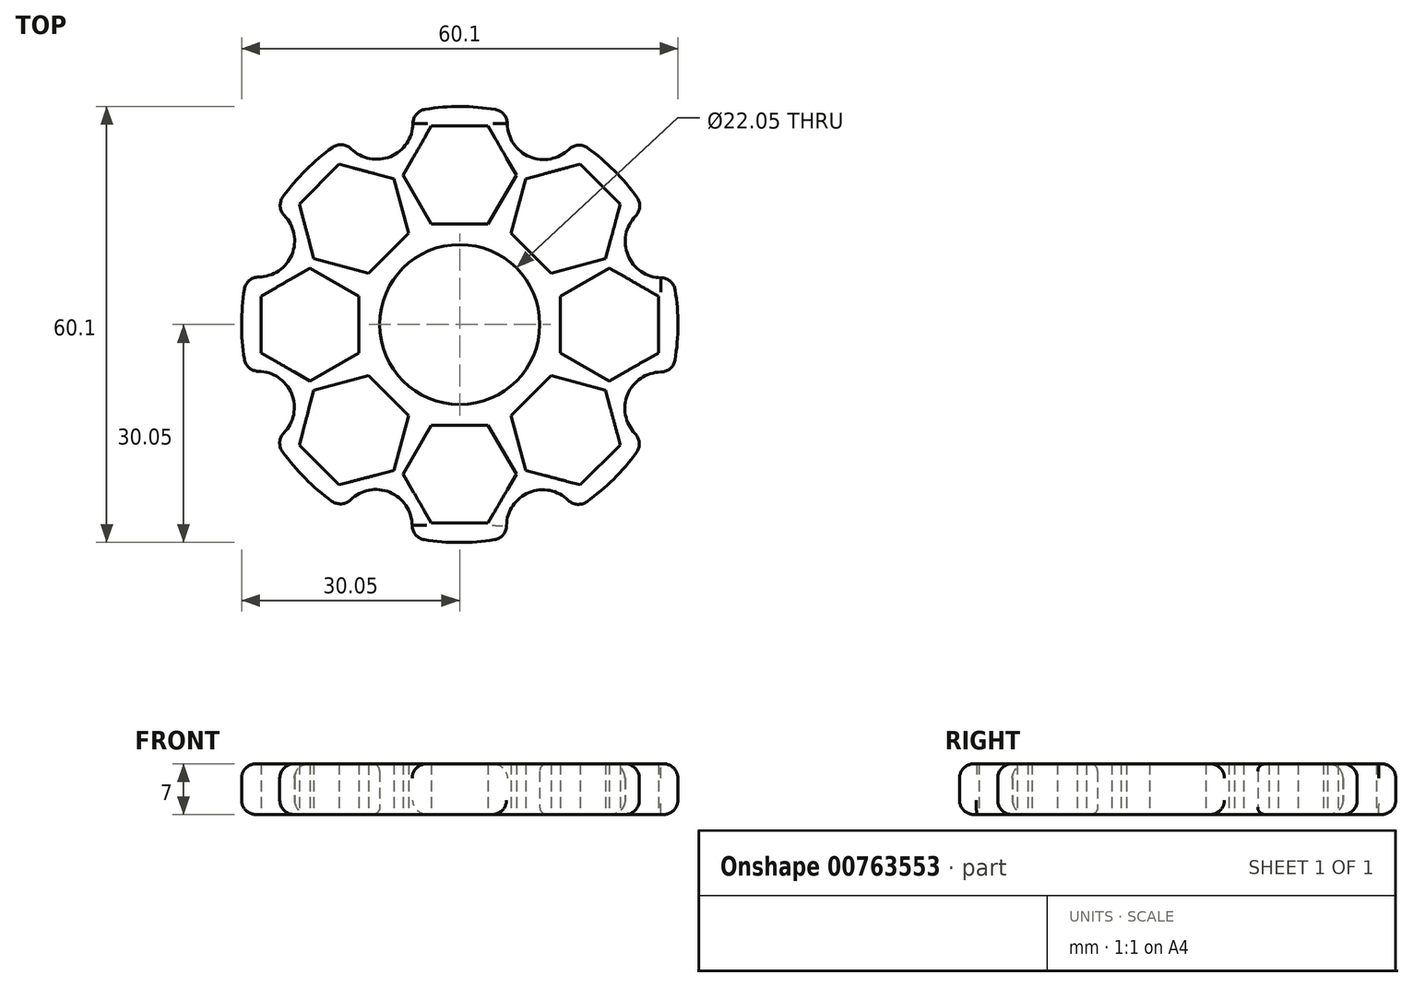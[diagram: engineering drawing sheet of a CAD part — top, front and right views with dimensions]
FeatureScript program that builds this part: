
annotation { "Feature Type Name" : "Feature", "Feature Type Description" : "" }
export const myFeature = defineFeature(function(context is Context, id is Id, definition is map)
    precondition{}
    {
        {
            var Q0;
            Q0=qCreatedBy(makeId("Top.planeOp"),FACE);
            var sketch = newSketch(context, id + "F0", { "sketchPlane" : qUnion([Q0])});
            skCircle(sketch, "E0", {"center": v(0, 0) * mm, "radius": 11.03 * mm});
            skCircle(sketch, "E1", {"center": v(0, 0) * mm, "radius": 13.53 * mm});
            skCircle(sketch, "E2", {"center": v(0, 0) * mm, "radius": 30.05 * mm});
            skLineSegment(sketch, "E3.0", {"start": v(3.9, 13.87) * mm, "end": v(-3.9, 13.87) * mm});
            skLineSegment(sketch, "E3.1", {"start": v(-3.9, 13.87) * mm, "end": v(-7.8, 20.62) * mm});
            skLineSegment(sketch, "E3.2", {"start": v(-7.8, 20.62) * mm, "end": v(-3.9, 27.37) * mm});
            skLineSegment(sketch, "E3.3", {"start": v(-3.9, 27.37) * mm, "end": v(3.9, 27.37) * mm});
            skLineSegment(sketch, "E3.4", {"start": v(3.9, 27.37) * mm, "end": v(7.8, 20.62) * mm});
            skLineSegment(sketch, "E3.5", {"start": v(7.8, 20.62) * mm, "end": v(3.9, 13.87) * mm});
            skPoint(sketch, "E3.0.midPoint", {"position": v(0, 13.87) * mm});
            skLineSegment(sketch, "E4.1.0", {"start": v(-9.07, 20.09) * mm, "end": v(-7.05, 12.56) * mm});
            skLineSegment(sketch, "E4.1.1", {"start": v(-20.09, 9.07) * mm, "end": v(-22.1, 16.6) * mm});
            skLineSegment(sketch, "E4.1.2", {"start": v(-12.56, 7.05) * mm, "end": v(-20.09, 9.07) * mm});
            skLineSegment(sketch, "E4.1.3", {"start": v(-7.05, 12.56) * mm, "end": v(-12.56, 7.05) * mm});
            skLineSegment(sketch, "E4.1.4", {"start": v(-22.1, 16.6) * mm, "end": v(-16.6, 22.1) * mm});
            skLineSegment(sketch, "E4.1.5", {"start": v(-16.6, 22.1) * mm, "end": v(-9.07, 20.09) * mm});
            skPoint(sketch, "E4.1.6", {"position": v(-9.8, 9.8) * mm});
            skLineSegment(sketch, "E4.2.0", {"start": v(-20.62, 7.8) * mm, "end": v(-13.87, 3.9) * mm});
            skLineSegment(sketch, "E4.2.1", {"start": v(-20.62, -7.8) * mm, "end": v(-27.37, -3.9) * mm});
            skLineSegment(sketch, "E4.2.2", {"start": v(-13.87, -3.9) * mm, "end": v(-20.62, -7.8) * mm});
            skLineSegment(sketch, "E4.2.3", {"start": v(-13.87, 3.9) * mm, "end": v(-13.87, -3.9) * mm});
            skLineSegment(sketch, "E4.2.4", {"start": v(-27.37, -3.9) * mm, "end": v(-27.37, 3.9) * mm});
            skLineSegment(sketch, "E4.2.5", {"start": v(-27.37, 3.9) * mm, "end": v(-20.62, 7.8) * mm});
            skPoint(sketch, "E4.2.6", {"position": v(-13.87, 0) * mm});
            skLineSegment(sketch, "E4.3.0", {"start": v(-20.09, -9.07) * mm, "end": v(-12.56, -7.05) * mm});
            skLineSegment(sketch, "E4.3.1", {"start": v(-9.07, -20.09) * mm, "end": v(-16.6, -22.1) * mm});
            skLineSegment(sketch, "E4.3.2", {"start": v(-7.05, -12.56) * mm, "end": v(-9.07, -20.09) * mm});
            skLineSegment(sketch, "E4.3.3", {"start": v(-12.56, -7.05) * mm, "end": v(-7.05, -12.56) * mm});
            skLineSegment(sketch, "E4.3.4", {"start": v(-16.6, -22.1) * mm, "end": v(-22.1, -16.6) * mm});
            skLineSegment(sketch, "E4.3.5", {"start": v(-22.1, -16.6) * mm, "end": v(-20.09, -9.07) * mm});
            skPoint(sketch, "E4.3.6", {"position": v(-9.8, -9.8) * mm});
            skLineSegment(sketch, "E4.4.0", {"start": v(-7.8, -20.62) * mm, "end": v(-3.9, -13.87) * mm});
            skLineSegment(sketch, "E4.4.1", {"start": v(7.8, -20.62) * mm, "end": v(3.9, -27.37) * mm});
            skLineSegment(sketch, "E4.4.2", {"start": v(3.9, -13.87) * mm, "end": v(7.8, -20.62) * mm});
            skLineSegment(sketch, "E4.4.3", {"start": v(-3.9, -13.87) * mm, "end": v(3.9, -13.87) * mm});
            skLineSegment(sketch, "E4.4.4", {"start": v(3.9, -27.37) * mm, "end": v(-3.9, -27.37) * mm});
            skLineSegment(sketch, "E4.4.5", {"start": v(-3.9, -27.37) * mm, "end": v(-7.8, -20.62) * mm});
            skPoint(sketch, "E4.4.6", {"position": v(0, -13.87) * mm});
            skLineSegment(sketch, "E4.5.0", {"start": v(9.07, -20.09) * mm, "end": v(7.05, -12.56) * mm});
            skLineSegment(sketch, "E4.5.1", {"start": v(20.09, -9.07) * mm, "end": v(22.1, -16.6) * mm});
            skLineSegment(sketch, "E4.5.2", {"start": v(12.56, -7.05) * mm, "end": v(20.09, -9.07) * mm});
            skLineSegment(sketch, "E4.5.3", {"start": v(7.05, -12.56) * mm, "end": v(12.56, -7.05) * mm});
            skLineSegment(sketch, "E4.5.4", {"start": v(22.1, -16.6) * mm, "end": v(16.6, -22.1) * mm});
            skLineSegment(sketch, "E4.5.5", {"start": v(16.6, -22.1) * mm, "end": v(9.07, -20.09) * mm});
            skPoint(sketch, "E4.5.6", {"position": v(9.8, -9.8) * mm});
            skLineSegment(sketch, "E4.6.0", {"start": v(20.62, -7.8) * mm, "end": v(13.87, -3.9) * mm});
            skLineSegment(sketch, "E4.6.1", {"start": v(20.62, 7.8) * mm, "end": v(27.37, 3.9) * mm});
            skLineSegment(sketch, "E4.6.2", {"start": v(13.87, 3.9) * mm, "end": v(20.62, 7.8) * mm});
            skLineSegment(sketch, "E4.6.3", {"start": v(13.87, -3.9) * mm, "end": v(13.87, 3.9) * mm});
            skLineSegment(sketch, "E4.6.4", {"start": v(27.37, 3.9) * mm, "end": v(27.37, -3.9) * mm});
            skLineSegment(sketch, "E4.6.5", {"start": v(27.37, -3.9) * mm, "end": v(20.62, -7.8) * mm});
            skPoint(sketch, "E4.6.6", {"position": v(13.87, 0) * mm});
            skLineSegment(sketch, "E4.7.0", {"start": v(20.09, 9.07) * mm, "end": v(12.56, 7.05) * mm});
            skLineSegment(sketch, "E4.7.1", {"start": v(9.07, 20.09) * mm, "end": v(16.6, 22.1) * mm});
            skLineSegment(sketch, "E4.7.2", {"start": v(7.05, 12.56) * mm, "end": v(9.07, 20.09) * mm});
            skLineSegment(sketch, "E4.7.3", {"start": v(12.56, 7.05) * mm, "end": v(7.05, 12.56) * mm});
            skLineSegment(sketch, "E4.7.4", {"start": v(16.6, 22.1) * mm, "end": v(22.1, 16.6) * mm});
            skLineSegment(sketch, "E4.7.5", {"start": v(22.1, 16.6) * mm, "end": v(20.09, 9.07) * mm});
            skPoint(sketch, "E4.7.6", {"position": v(9.8, 9.8) * mm});
            skPoint(sketch, "E5.centerSnap0", {"position": v(-11.44, 27.63) * mm});
            skCircle(sketch, "E6", {"center": v(-11.44, 27.78) * mm, "radius": 5 * mm});
            skCircle(sketch, "E7.1.0", {"center": v(-27.74, 11.55) * mm, "radius": 5 * mm});
            skCircle(sketch, "E7.2.0", {"center": v(-27.78, -11.44) * mm, "radius": 5 * mm});
            skCircle(sketch, "E7.3.0", {"center": v(-11.55, -27.74) * mm, "radius": 5 * mm});
            skCircle(sketch, "E7.4.0", {"center": v(11.44, -27.78) * mm, "radius": 5 * mm});
            skCircle(sketch, "E7.5.0", {"center": v(27.74, -11.55) * mm, "radius": 5 * mm});
            skCircle(sketch, "E7.6.0", {"center": v(27.78, 11.44) * mm, "radius": 5 * mm});
            skCircle(sketch, "E7.7.0", {"center": v(11.55, 27.74) * mm, "radius": 5 * mm});
            skSolve(sketch);
        }
        {
            var Q0;
            Q0=makeQuery(id+"F0.imprint","IMPRINT",FACE,{"disambiguationData":[TD([[makeQuery(id+"F0.imprint","IMPRINT",EDGE,{"derivedFrom":sQuery(id+"F0.wireOp",EDGE,"E1")}),-1.0]])]});
            var Q1;
            Q1=makeQuery(id+"F0.imprint","IMPRINT",FACE,{"disambiguationData":[TD([[makeQuery(id+"F0.imprint","IMPRINT",EDGE,{"derivedFrom":sQuery(id+"F0.wireOp",EDGE,"E0")}),-1.0]])]});
            extrude(context, id + "F1", {"entities" : qUnion([Q0, Q1]), "depth" : 7 * mm, "offsetDistance" : 25 * mm});
        }
        {
            var Q0;
            {var subQ0=sQuery(id+"F0.wireOp",EDGE,"E2");Q0=makeQuery(id+"F1.opExtrude","CAP_EDGE",EDGE,{"disambiguationData":[OSD([subQ0]),TDD([makeQuery(id+"F0.imprint","IMPRINT",EDGE,{"disambiguationData":[TD([[makeQuery(id+"F0.imprint","INTERSECT",VERTEX,{"disambiguationData":[OD(1.0)],"derivedFrom":[subQ0,sQuery(id+"F0.wireOp",EDGE,"E7.3.0")]}),-1.0]])],"derivedFrom":subQ0})])],"isStart":true});}
            var Q1;
            Q1=makeQuery(id+"F1.opExtrude","CAP_EDGE",EDGE,{"disambiguationData":[OSD([sQuery(id+"F0.wireOp",EDGE,"E7.3.0")])],"isStart":true});
            var Q2;
            Q2=makeQuery(id+"F1.opExtrude","CAP_EDGE",EDGE,{"disambiguationData":[OSD([sQuery(id+"F0.wireOp",EDGE,"E7.2.0")])],"isStart":true});
            var Q3;
            {var subQ0=sQuery(id+"F0.wireOp",EDGE,"E2");Q3=makeQuery(id+"F1.opExtrude","CAP_EDGE",EDGE,{"disambiguationData":[OSD([subQ0]),TDD([makeQuery(id+"F0.imprint","IMPRINT",EDGE,{"disambiguationData":[TD([[makeQuery(id+"F0.imprint","INTERSECT",VERTEX,{"disambiguationData":[OD(1.0)],"derivedFrom":[subQ0,sQuery(id+"F0.wireOp",EDGE,"E7.1.0")]}),-1.0]])],"derivedFrom":subQ0})])],"isStart":true});}
            var Q4;
            {var subQ0=sQuery(id+"F0.wireOp",EDGE,"E7.1.0");var subQ1=sQuery(id+"F0.wireOp",EDGE,"E2");Q4=makeQuery(id+"F1.opExtrude","SWEPT_EDGE",EDGE,{"disambiguationData":[OSD([subQ1,subQ0]),TDD([makeQuery(id+"F0.imprint","INTERSECT",VERTEX,{"disambiguationData":[OD(0.0)],"derivedFrom":[subQ1,subQ0]})])]});}
            var Q5;
            {var subQ0=sQuery(id+"F0.wireOp",EDGE,"E7.1.0");var subQ1=sQuery(id+"F0.wireOp",EDGE,"E2");Q5=makeQuery(id+"F1.opExtrude","SWEPT_EDGE",EDGE,{"disambiguationData":[OSD([subQ1,subQ0]),TDD([makeQuery(id+"F0.imprint","INTERSECT",VERTEX,{"disambiguationData":[OD(1.0)],"derivedFrom":[subQ1,subQ0]})])]});}
            var Q6;
            {var subQ0=sQuery(id+"F0.wireOp",EDGE,"E2");Q6=makeQuery(id+"F1.opExtrude","CAP_EDGE",EDGE,{"disambiguationData":[OSD([subQ0]),TDD([makeQuery(id+"F0.imprint","IMPRINT",EDGE,{"disambiguationData":[TD([[makeQuery(id+"F0.imprint","INTERSECT",VERTEX,{"disambiguationData":[OD(1.0)],"derivedFrom":[subQ0,sQuery(id+"F0.wireOp",EDGE,"E7.2.0")]}),-1.0]])],"derivedFrom":subQ0})])],"isStart":true});}
            var Q7;
            Q7=makeQuery(id+"F1.opExtrude","CAP_EDGE",EDGE,{"disambiguationData":[OSD([sQuery(id+"F0.wireOp",EDGE,"E7.1.0")])],"isStart":true});
            var Q8;
            {var subQ0=sQuery(id+"F0.wireOp",EDGE,"E2");Q8=makeQuery(id+"F1.opExtrude","CAP_EDGE",EDGE,{"disambiguationData":[OSD([subQ0]),TDD([makeQuery(id+"F0.imprint","IMPRINT",EDGE,{"disambiguationData":[TD([[makeQuery(id+"F0.imprint","INTERSECT",VERTEX,{"disambiguationData":[OD(1.0)],"derivedFrom":[subQ0,sQuery(id+"F0.wireOp",EDGE,"E6")]}),-1.0]])],"derivedFrom":subQ0})])],"isStart":true});}
            var Q9;
            Q9=makeQuery(id+"F1.opExtrude","CAP_EDGE",EDGE,{"disambiguationData":[OSD([sQuery(id+"F0.wireOp",EDGE,"E6")])],"isStart":true});
            var Q10;
            {var subQ0=sQuery(id+"F0.wireOp",EDGE,"E2");Q10=makeQuery(id+"F1.opExtrude","CAP_EDGE",EDGE,{"disambiguationData":[OSD([subQ0]),TDD([makeQuery(id+"F0.imprint","IMPRINT",EDGE,{"disambiguationData":[TD([[makeQuery(id+"F0.imprint","INTERSECT",VERTEX,{"disambiguationData":[OD(1.0)],"derivedFrom":[subQ0,sQuery(id+"F0.wireOp",EDGE,"E7.7.0")]}),-1.0]])],"derivedFrom":subQ0})])],"isStart":true});}
            var Q11;
            Q11=makeQuery(id+"F1.opExtrude","CAP_EDGE",EDGE,{"disambiguationData":[OSD([sQuery(id+"F0.wireOp",EDGE,"E7.7.0")])],"isStart":true});
            var Q12;
            {var subQ0=sQuery(id+"F0.wireOp",EDGE,"E2");Q12=makeQuery(id+"F1.opExtrude","CAP_EDGE",EDGE,{"disambiguationData":[OSD([subQ0]),TDD([makeQuery(id+"F0.imprint","IMPRINT",EDGE,{"disambiguationData":[TD([[makeQuery(id+"F0.imprint","INTERSECT",VERTEX,{"disambiguationData":[OD(0.0)],"derivedFrom":[subQ0,sQuery(id+"F0.wireOp",EDGE,"E7.6.0")]}),-1.0]])],"derivedFrom":subQ0})])],"isStart":true});}
            var Q13;
            Q13=makeQuery(id+"F1.opExtrude","CAP_EDGE",EDGE,{"disambiguationData":[OSD([sQuery(id+"F0.wireOp",EDGE,"E7.6.0")])],"isStart":true});
            var Q14;
            {var subQ0=sQuery(id+"F0.wireOp",EDGE,"E2");Q14=makeQuery(id+"F1.opExtrude","CAP_EDGE",EDGE,{"disambiguationData":[OSD([subQ0]),TDD([makeQuery(id+"F0.imprint","IMPRINT",EDGE,{"disambiguationData":[TD([[makeQuery(id+"F0.imprint","INTERSECT",VERTEX,{"disambiguationData":[OD(1.0)],"derivedFrom":[subQ0,sQuery(id+"F0.wireOp",EDGE,"E7.6.0")]}),1.0]])],"derivedFrom":subQ0})])],"isStart":true});}
            var Q15;
            Q15=makeQuery(id+"F1.opExtrude","CAP_EDGE",EDGE,{"disambiguationData":[OSD([sQuery(id+"F0.wireOp",EDGE,"E7.5.0")])],"isStart":true});
            var Q16;
            {var subQ0=sQuery(id+"F0.wireOp",EDGE,"E2");Q16=makeQuery(id+"F1.opExtrude","CAP_EDGE",EDGE,{"disambiguationData":[OSD([subQ0]),TDD([makeQuery(id+"F0.imprint","IMPRINT",EDGE,{"disambiguationData":[TD([[makeQuery(id+"F0.imprint","INTERSECT",VERTEX,{"disambiguationData":[OD(1.0)],"derivedFrom":[subQ0,sQuery(id+"F0.wireOp",EDGE,"E7.4.0")]}),-1.0]])],"derivedFrom":subQ0})])],"isStart":true});}
            var Q17;
            Q17=makeQuery(id+"F1.opExtrude","CAP_EDGE",EDGE,{"disambiguationData":[OSD([sQuery(id+"F0.wireOp",EDGE,"E7.4.0")])],"isStart":true});
            var Q18;
            {var subQ0=sQuery(id+"F0.wireOp",EDGE,"E2");Q18=makeQuery(id+"F1.opExtrude","CAP_EDGE",EDGE,{"disambiguationData":[OSD([subQ0]),TDD([makeQuery(id+"F0.imprint","IMPRINT",EDGE,{"disambiguationData":[TD([[makeQuery(id+"F0.imprint","INTERSECT",VERTEX,{"disambiguationData":[OD(1.0)],"derivedFrom":[subQ0,sQuery(id+"F0.wireOp",EDGE,"E7.7.0")]}),-1.0]])],"derivedFrom":subQ0})])],"isStart":false});}
            var Q19;
            Q19=makeQuery(id+"F1.opExtrude","CAP_EDGE",EDGE,{"disambiguationData":[OSD([sQuery(id+"F0.wireOp",EDGE,"E7.7.0")])],"isStart":false});
            var Q20;
            Q20=makeQuery(id+"F1.opExtrude","CAP_EDGE",EDGE,{"disambiguationData":[OSD([sQuery(id+"F0.wireOp",EDGE,"E7.6.0")])],"isStart":false});
            var Q21;
            {var subQ0=sQuery(id+"F0.wireOp",EDGE,"E2");Q21=makeQuery(id+"F1.opExtrude","CAP_EDGE",EDGE,{"disambiguationData":[OSD([subQ0]),TDD([makeQuery(id+"F0.imprint","IMPRINT",EDGE,{"disambiguationData":[TD([[makeQuery(id+"F0.imprint","INTERSECT",VERTEX,{"disambiguationData":[OD(0.0)],"derivedFrom":[subQ0,sQuery(id+"F0.wireOp",EDGE,"E7.6.0")]}),-1.0]])],"derivedFrom":subQ0})])],"isStart":false});}
            var Q22;
            Q22=makeQuery(id+"F1.opExtrude","CAP_EDGE",EDGE,{"disambiguationData":[OSD([sQuery(id+"F0.wireOp",EDGE,"E6")])],"isStart":false});
            var Q23;
            {var subQ0=sQuery(id+"F0.wireOp",EDGE,"E2");Q23=makeQuery(id+"F1.opExtrude","CAP_EDGE",EDGE,{"disambiguationData":[OSD([subQ0]),TDD([makeQuery(id+"F0.imprint","IMPRINT",EDGE,{"disambiguationData":[TD([[makeQuery(id+"F0.imprint","INTERSECT",VERTEX,{"disambiguationData":[OD(1.0)],"derivedFrom":[subQ0,sQuery(id+"F0.wireOp",EDGE,"E6")]}),-1.0]])],"derivedFrom":subQ0})])],"isStart":false});}
            var Q24;
            Q24=makeQuery(id+"F1.opExtrude","CAP_EDGE",EDGE,{"disambiguationData":[OSD([sQuery(id+"F0.wireOp",EDGE,"E7.1.0")])],"isStart":false});
            var Q25;
            {var subQ0=sQuery(id+"F0.wireOp",EDGE,"E2");Q25=makeQuery(id+"F1.opExtrude","CAP_EDGE",EDGE,{"disambiguationData":[OSD([subQ0]),TDD([makeQuery(id+"F0.imprint","IMPRINT",EDGE,{"disambiguationData":[TD([[makeQuery(id+"F0.imprint","INTERSECT",VERTEX,{"disambiguationData":[OD(1.0)],"derivedFrom":[subQ0,sQuery(id+"F0.wireOp",EDGE,"E7.1.0")]}),-1.0]])],"derivedFrom":subQ0})])],"isStart":false});}
            var Q26;
            Q26=makeQuery(id+"F1.opExtrude","CAP_EDGE",EDGE,{"disambiguationData":[OSD([sQuery(id+"F0.wireOp",EDGE,"E7.2.0")])],"isStart":false});
            var Q27;
            {var subQ0=sQuery(id+"F0.wireOp",EDGE,"E2");Q27=makeQuery(id+"F1.opExtrude","CAP_EDGE",EDGE,{"disambiguationData":[OSD([subQ0]),TDD([makeQuery(id+"F0.imprint","IMPRINT",EDGE,{"disambiguationData":[TD([[makeQuery(id+"F0.imprint","INTERSECT",VERTEX,{"disambiguationData":[OD(1.0)],"derivedFrom":[subQ0,sQuery(id+"F0.wireOp",EDGE,"E7.2.0")]}),-1.0]])],"derivedFrom":subQ0})])],"isStart":false});}
            var Q28;
            Q28=makeQuery(id+"F1.opExtrude","CAP_EDGE",EDGE,{"disambiguationData":[OSD([sQuery(id+"F0.wireOp",EDGE,"E7.3.0")])],"isStart":false});
            var Q29;
            {var subQ0=sQuery(id+"F0.wireOp",EDGE,"E2");Q29=makeQuery(id+"F1.opExtrude","CAP_EDGE",EDGE,{"disambiguationData":[OSD([subQ0]),TDD([makeQuery(id+"F0.imprint","IMPRINT",EDGE,{"disambiguationData":[TD([[makeQuery(id+"F0.imprint","INTERSECT",VERTEX,{"disambiguationData":[OD(1.0)],"derivedFrom":[subQ0,sQuery(id+"F0.wireOp",EDGE,"E7.3.0")]}),-1.0]])],"derivedFrom":subQ0})])],"isStart":false});}
            var Q30;
            Q30=makeQuery(id+"F1.opExtrude","CAP_EDGE",EDGE,{"disambiguationData":[OSD([sQuery(id+"F0.wireOp",EDGE,"E7.4.0")])],"isStart":false});
            var Q31;
            {var subQ0=sQuery(id+"F0.wireOp",EDGE,"E2");Q31=makeQuery(id+"F1.opExtrude","CAP_EDGE",EDGE,{"disambiguationData":[OSD([subQ0]),TDD([makeQuery(id+"F0.imprint","IMPRINT",EDGE,{"disambiguationData":[TD([[makeQuery(id+"F0.imprint","INTERSECT",VERTEX,{"disambiguationData":[OD(1.0)],"derivedFrom":[subQ0,sQuery(id+"F0.wireOp",EDGE,"E7.4.0")]}),-1.0]])],"derivedFrom":subQ0})])],"isStart":false});}
            var Q32;
            Q32=makeQuery(id+"F1.opExtrude","CAP_EDGE",EDGE,{"disambiguationData":[OSD([sQuery(id+"F0.wireOp",EDGE,"E7.5.0")])],"isStart":false});
            var Q33;
            {var subQ0=sQuery(id+"F0.wireOp",EDGE,"E2");Q33=makeQuery(id+"F1.opExtrude","CAP_EDGE",EDGE,{"disambiguationData":[OSD([subQ0]),TDD([makeQuery(id+"F0.imprint","IMPRINT",EDGE,{"disambiguationData":[TD([[makeQuery(id+"F0.imprint","INTERSECT",VERTEX,{"disambiguationData":[OD(1.0)],"derivedFrom":[subQ0,sQuery(id+"F0.wireOp",EDGE,"E7.6.0")]}),1.0]])],"derivedFrom":subQ0})])],"isStart":false});}
            var Q34;
            {var subQ0=sQuery(id+"F0.wireOp",EDGE,"E7.4.0");var subQ1=sQuery(id+"F0.wireOp",EDGE,"E2");Q34=makeQuery(id+"F1.opExtrude","SWEPT_EDGE",EDGE,{"disambiguationData":[OSD([subQ1,subQ0]),TDD([makeQuery(id+"F0.imprint","INTERSECT",VERTEX,{"disambiguationData":[OD(0.0)],"derivedFrom":[subQ1,subQ0]})])]});}
            var Q35;
            {var subQ0=sQuery(id+"F0.wireOp",EDGE,"E7.3.0");var subQ1=sQuery(id+"F0.wireOp",EDGE,"E2");Q35=makeQuery(id+"F1.opExtrude","SWEPT_EDGE",EDGE,{"disambiguationData":[OSD([subQ1,subQ0]),TDD([makeQuery(id+"F0.imprint","INTERSECT",VERTEX,{"disambiguationData":[OD(1.0)],"derivedFrom":[subQ1,subQ0]})])]});}
            var Q36;
            {var subQ0=sQuery(id+"F0.wireOp",EDGE,"E7.4.0");var subQ1=sQuery(id+"F0.wireOp",EDGE,"E2");Q36=makeQuery(id+"F1.opExtrude","SWEPT_EDGE",EDGE,{"disambiguationData":[OSD([subQ1,subQ0]),TDD([makeQuery(id+"F0.imprint","INTERSECT",VERTEX,{"disambiguationData":[OD(1.0)],"derivedFrom":[subQ1,subQ0]})])]});}
            var Q37;
            {var subQ0=sQuery(id+"F0.wireOp",EDGE,"E7.3.0");var subQ1=sQuery(id+"F0.wireOp",EDGE,"E2");Q37=makeQuery(id+"F1.opExtrude","SWEPT_EDGE",EDGE,{"disambiguationData":[OSD([subQ1,subQ0]),TDD([makeQuery(id+"F0.imprint","INTERSECT",VERTEX,{"disambiguationData":[OD(0.0)],"derivedFrom":[subQ1,subQ0]})])]});}
            var Q38;
            {var subQ0=sQuery(id+"F0.wireOp",EDGE,"E7.2.0");var subQ1=sQuery(id+"F0.wireOp",EDGE,"E2");Q38=makeQuery(id+"F1.opExtrude","SWEPT_EDGE",EDGE,{"disambiguationData":[OSD([subQ1,subQ0]),TDD([makeQuery(id+"F0.imprint","INTERSECT",VERTEX,{"disambiguationData":[OD(1.0)],"derivedFrom":[subQ1,subQ0]})])]});}
            var Q39;
            {var subQ0=sQuery(id+"F0.wireOp",EDGE,"E7.2.0");var subQ1=sQuery(id+"F0.wireOp",EDGE,"E2");Q39=makeQuery(id+"F1.opExtrude","SWEPT_EDGE",EDGE,{"disambiguationData":[OSD([subQ1,subQ0]),TDD([makeQuery(id+"F0.imprint","INTERSECT",VERTEX,{"disambiguationData":[OD(0.0)],"derivedFrom":[subQ1,subQ0]})])]});}
            var Q40;
            {var subQ0=sQuery(id+"F0.wireOp",EDGE,"E6");var subQ1=sQuery(id+"F0.wireOp",EDGE,"E2");Q40=makeQuery(id+"F1.opExtrude","SWEPT_EDGE",EDGE,{"disambiguationData":[OSD([subQ1,subQ0]),TDD([makeQuery(id+"F0.imprint","INTERSECT",VERTEX,{"disambiguationData":[OD(1.0)],"derivedFrom":[subQ1,subQ0]})])]});}
            var Q41;
            {var subQ0=sQuery(id+"F0.wireOp",EDGE,"E6");var subQ1=sQuery(id+"F0.wireOp",EDGE,"E2");Q41=makeQuery(id+"F1.opExtrude","SWEPT_EDGE",EDGE,{"disambiguationData":[OSD([subQ1,subQ0]),TDD([makeQuery(id+"F0.imprint","INTERSECT",VERTEX,{"disambiguationData":[OD(0.0)],"derivedFrom":[subQ1,subQ0]})])]});}
            var Q42;
            {var subQ0=sQuery(id+"F0.wireOp",EDGE,"E7.7.0");var subQ1=sQuery(id+"F0.wireOp",EDGE,"E2");Q42=makeQuery(id+"F1.opExtrude","SWEPT_EDGE",EDGE,{"disambiguationData":[OSD([subQ1,subQ0]),TDD([makeQuery(id+"F0.imprint","INTERSECT",VERTEX,{"disambiguationData":[OD(1.0)],"derivedFrom":[subQ1,subQ0]})])]});}
            var Q43;
            {var subQ0=sQuery(id+"F0.wireOp",EDGE,"E7.5.0");var subQ1=sQuery(id+"F0.wireOp",EDGE,"E2");Q43=makeQuery(id+"F1.opExtrude","SWEPT_EDGE",EDGE,{"disambiguationData":[OSD([subQ1,subQ0]),TDD([makeQuery(id+"F0.imprint","INTERSECT",VERTEX,{"disambiguationData":[OD(1.0)],"derivedFrom":[subQ1,subQ0]})])]});}
            var Q44;
            {var subQ0=sQuery(id+"F0.wireOp",EDGE,"E7.5.0");var subQ1=sQuery(id+"F0.wireOp",EDGE,"E2");Q44=makeQuery(id+"F1.opExtrude","SWEPT_EDGE",EDGE,{"disambiguationData":[OSD([subQ1,subQ0]),TDD([makeQuery(id+"F0.imprint","INTERSECT",VERTEX,{"disambiguationData":[OD(0.0)],"derivedFrom":[subQ1,subQ0]})])]});}
            var Q45;
            {var subQ0=sQuery(id+"F0.wireOp",EDGE,"E7.6.0");var subQ1=sQuery(id+"F0.wireOp",EDGE,"E2");Q45=makeQuery(id+"F1.opExtrude","SWEPT_EDGE",EDGE,{"disambiguationData":[OSD([subQ1,subQ0]),TDD([makeQuery(id+"F0.imprint","INTERSECT",VERTEX,{"disambiguationData":[OD(1.0)],"derivedFrom":[subQ1,subQ0]})])]});}
            var Q46;
            {var subQ0=sQuery(id+"F0.wireOp",EDGE,"E7.6.0");var subQ1=sQuery(id+"F0.wireOp",EDGE,"E2");Q46=makeQuery(id+"F1.opExtrude","SWEPT_EDGE",EDGE,{"disambiguationData":[OSD([subQ1,subQ0]),TDD([makeQuery(id+"F0.imprint","INTERSECT",VERTEX,{"disambiguationData":[OD(0.0)],"derivedFrom":[subQ1,subQ0]})])]});}
            var Q47;
            {var subQ0=sQuery(id+"F0.wireOp",EDGE,"E7.7.0");var subQ1=sQuery(id+"F0.wireOp",EDGE,"E2");Q47=makeQuery(id+"F1.opExtrude","SWEPT_EDGE",EDGE,{"disambiguationData":[OSD([subQ1,subQ0]),TDD([makeQuery(id+"F0.imprint","INTERSECT",VERTEX,{"disambiguationData":[OD(0.0)],"derivedFrom":[subQ1,subQ0]})])]});}
            fillet(context, id + "F2", {"entities" : qUnion([Q0, Q1, Q2, Q3, Q4, Q5, Q6, Q7, Q8, Q9, Q10, Q11, Q12, Q13, Q14, Q15, Q16, Q17, Q18, Q19, Q20, Q21, Q22, Q23, Q24, Q25, Q26, Q27, Q28, Q29, Q30, Q31, Q32, Q33, Q34, Q35, Q36, Q37, Q38, Q39, Q40, Q41, Q42, Q43, Q44, Q45, Q46, Q47]), "radius" : 2 * mm, "tangentPropagation" : true, "allowEdgeOverflow" : false});
        }
        {
            var Q0;
            Q0=makeQuery(id+"F1.opExtrude","CAP_EDGE",EDGE,{"disambiguationData":[OSD([sQuery(id+"F0.wireOp",EDGE,"E0")])],"isStart":true});
            var Q1;
            Q1=makeQuery(id+"F1.opExtrude","CAP_EDGE",EDGE,{"disambiguationData":[OSD([sQuery(id+"F0.wireOp",EDGE,"E0")])],"isStart":false});
            fillet(context, id + "F3", {"entities" : qUnion([Q0, Q1]), "radius" : 1 * mm, "tangentPropagation" : true, "allowEdgeOverflow" : false});
        }
    });
